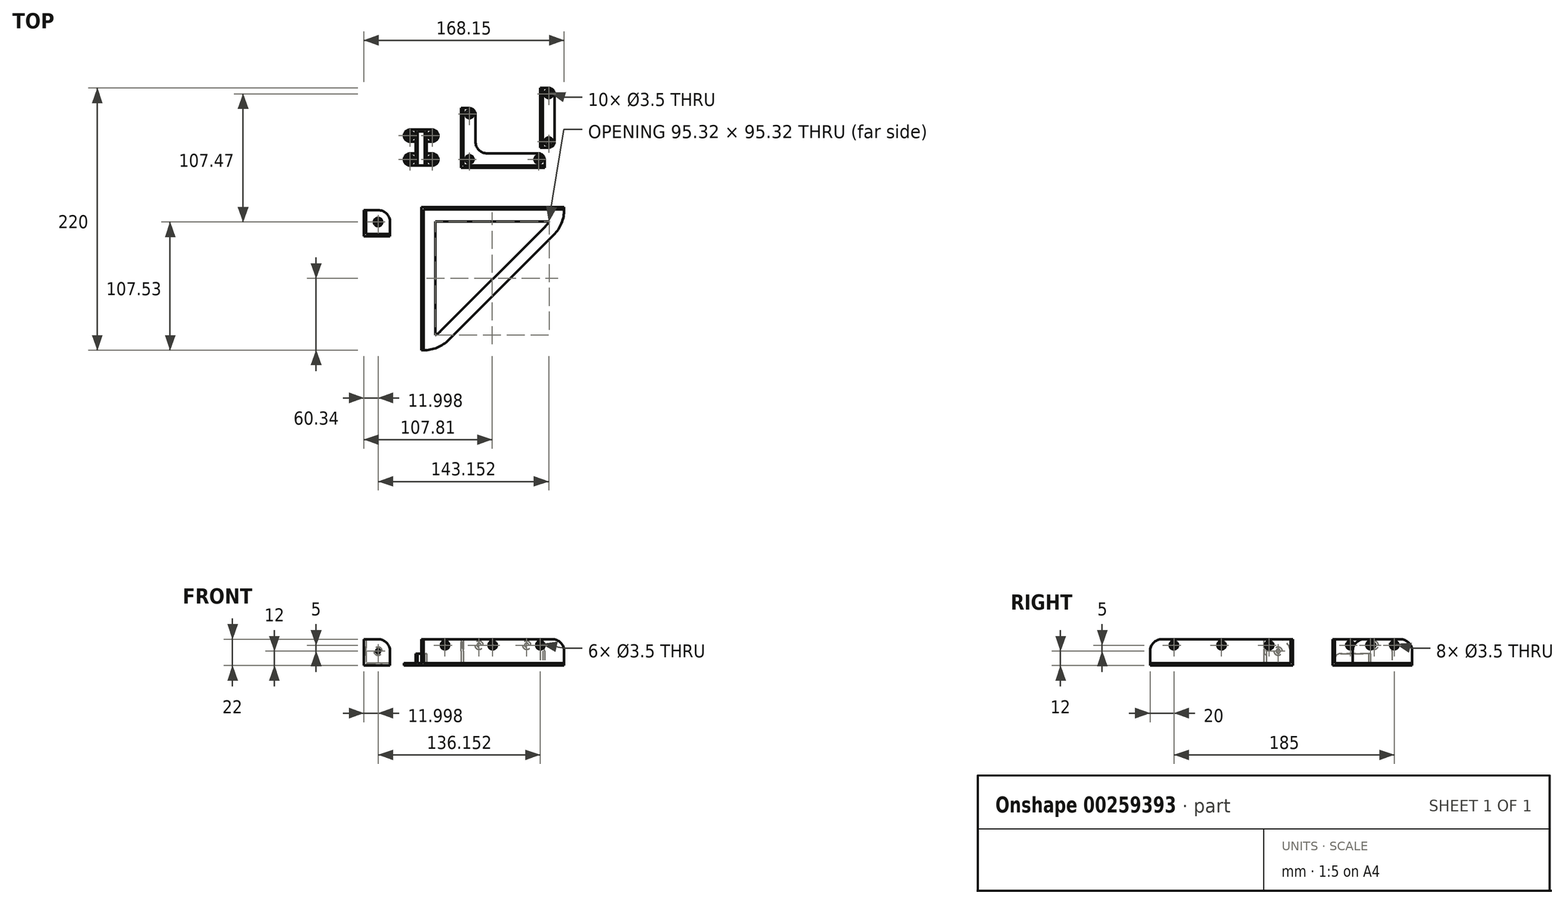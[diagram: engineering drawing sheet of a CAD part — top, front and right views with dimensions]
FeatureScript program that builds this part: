
annotation { "Feature Type Name" : "Feature", "Feature Type Description" : "" }
export const myFeature = defineFeature(function(context is Context, id is Id, definition is map)
    precondition{}
    {
        {
            var Q0;
            Q0=qCreatedBy(makeId("Top.planeOp"),FACE);
            var sketch = newSketch(context, id + "F0", { "sketchPlane" : qUnion([Q0])});
            skLineSegment(sketch, "E0.bottom", {"start": v(-4.5, 15) * mm, "end": v(4.5, 15) * mm});
            skLineSegment(sketch, "E0.top", {"start": v(-4.5, -15) * mm, "end": v(4.5, -15) * mm});
            skLineSegment(sketch, "E0.left", {"start": v(-4.5, 15) * mm, "end": v(-4.5, -15) * mm});
            skLineSegment(sketch, "E0.right", {"start": v(4.5, 15) * mm, "end": v(4.5, -15) * mm});
            skLineSegment(sketch, "E1", {"start": v(-2.9, 13.4) * mm, "end": v(-2.9, -15) * mm});
            skLineSegment(sketch, "E2", {"start": v(2.9, -15) * mm, "end": v(2.9, 13.4) * mm});
            skPoint(sketch, "E3", {"position": v(0, -15) * mm});
            skArc(sketch, "E4", {"start": v(9.5, -15) * mm, "mid": v(14.5, -10) * mm, "end": v(9.5, -5) * mm});
            skLineSegment(sketch, "E5", {"start": v(9.5, -5) * mm, "end": v(4.5, -5) * mm});
            skLineSegment(sketch, "E6", {"start": v(4.5, -15) * mm, "end": v(9.5, -15) * mm});
            skArc(sketch, "E7", {"start": v(9.5, 5) * mm, "mid": v(14.5, 10) * mm, "end": v(9.5, 15) * mm});
            skLineSegment(sketch, "E8", {"start": v(4.5, 15) * mm, "end": v(9.5, 15) * mm});
            skLineSegment(sketch, "E9", {"start": v(9.5, 5) * mm, "end": v(4.5, 5) * mm});
            skLineSegment(sketch, "E10", {"start": v(-2.9, 13.4) * mm, "end": v(2.9, 13.4) * mm});
            skSolve(sketch);
        }
        {
            var Q0;
            Q0 = qSketchRegion(id + "F0", true);
            extrude(context, id + "F1", {"entities" : qUnion([Q0]), "depth" : 2 * mm});
        }
        {
            var Q0;
            {var subQ6=sQuery(id+"F0.wireOp",EDGE,"E0.bottom");Q0=makeQuery(id+"F0.imprint","IMPRINT",FACE,{"disambiguationData":[TD([[makeQuery(id+"F0.imprint","IMPRINT",EDGE,{"derivedFrom":subQ6}),-1.0]])]});}
            extrude(context, id + "F2", {"entities" : qUnion([Q0]), "operationType" : NewBodyOperationType.ADD, "depth" : 10 * mm});
        }
        {
            var Q0;
            {var subQ0=sQuery(id+"F0.wireOp",EDGE,"E9");var subQ1=sQuery(id+"F0.wireOp",EDGE,"E7");var subQ2=sQuery(id+"F0.wireOp",EDGE,"E0.right");var subQ3=sQuery(id+"F0.wireOp",EDGE,"E8");var subQ4=sQuery(id+"F0.wireOp",EDGE,"E0.bottom");Q0=makeQuery(id+"F2.boolean.opBoolean","SPLIT",FACE,{"disambiguationData":[TD([makeQuery(id+"F1.opExtrude","SWEPT_FACE",FACE,{"disambiguationData":[OSD([subQ1])]})])],"derivedFrom":makeQuery(id+"F1.opExtrude","CAP_FACE",FACE,{"disambiguationData":[OSD([subQ4,sQuery(id+"F0.wireOp",EDGE,"E0.top"),sQuery(id+"F0.wireOp",EDGE,"E0.left"),subQ2,sQuery(id+"F0.wireOp",EDGE,"E4"),sQuery(id+"F0.wireOp",EDGE,"E5"),sQuery(id+"F0.wireOp",EDGE,"E6"),subQ1,subQ3,subQ0])],"isStart":false})});}
            var sketch = newSketch(context, id + "F3", { "sketchPlane" : qUnion([Q0])});
            skArc(sketch, "E11.0", {"start": v(9.5, 5) * mm, "mid": v(14.5, 10) * mm, "end": v(9.5, 15) * mm, "construction": true});
            skArc(sketch, "E12.0", {"start": v(9.5, -15) * mm, "mid": v(14.5, -10) * mm, "end": v(9.5, -5) * mm, "construction": true});
            skSolve(sketch);
        }
        {
            var Q0;
            {var subQ0=sQuery(id+"F0.wireOp",EDGE,"E0.top");Q0=makeQuery(id+"F2.opExtrude","CAP_EDGE",EDGE,{"disambiguationData":[OSD([subQ0]),TDD([makeQuery(id+"F0.imprint","IMPRINT",EDGE,{"disambiguationData":[TD([[makeQuery(id+"F0.imprint","INTERSECT",VERTEX,{"derivedFrom":[subQ0,sQuery(id+"F0.wireOp",EDGE,"E0.left")]}),-1.0]])],"derivedFrom":subQ0})])],"isStart":false});}
            var Q1;
            {var subQ0=sQuery(id+"F0.wireOp",EDGE,"E0.top");Q1=makeQuery(id+"F2.opExtrude","CAP_EDGE",EDGE,{"disambiguationData":[OSD([subQ0]),TDD([makeQuery(id+"F0.imprint","IMPRINT",EDGE,{"disambiguationData":[TD([[makeQuery(id+"F0.imprint","INTERSECT",VERTEX,{"derivedFrom":[subQ0,sQuery(id+"F0.wireOp",EDGE,"E2")]}),-1.0]])],"derivedFrom":subQ0})])],"isStart":false});}
            fillet(context, id + "F4", {"entities" : qUnion([Q0, Q1]), "radius" : 5 * mm, "tangentPropagation" : true, "allowEdgeOverflow" : false});
        }
        {
            var Q0;
            Q0=makeQuery(id+"F2.opExtrude","SWEPT_EDGE",EDGE,{"disambiguationData":[OSD([sQuery(id+"F0.wireOp",EDGE,"E0.bottom"),sQuery(id+"F0.wireOp",EDGE,"E0.right"),sQuery(id+"F0.wireOp",EDGE,"E8")])]});
            var Q1;
            {var subQ0=sQuery(id+"F0.wireOp",EDGE,"E0.left");var subQ1=sQuery(id+"F0.wireOp",EDGE,"E0.bottom");Q1=makeQuery(id+"F2.boolean.opBoolean","MERGE",EDGE,{"derivedFrom":[makeQuery(id+"F1.opExtrude","SWEPT_EDGE",EDGE,{"disambiguationData":[OSD([subQ1,subQ0])]}),makeQuery(id+"F2.opExtrude","SWEPT_EDGE",EDGE,{"disambiguationData":[OSD([subQ1,subQ0])]})]});}
            fillet(context, id + "F5", {"entities" : qUnion([Q0, Q1]), "radius" : 1 * mm, "tangentPropagation" : true, "allowEdgeOverflow" : false});
        }
        {
            var Q0;
            Q0=sQuery(id+"F3.wireOp",VERTEX,"E11.0.center");
            var Q1;
            Q1=sQuery(id+"F3.wireOp",VERTEX,"E12.0.center");
            var Q2;
            Q2=makeQuery(id+"F1.opExtrude","SWEPT_BODY",BODY,{"disambiguationData":[OSD([sQuery(id+"F0.wireOp",EDGE,"E0.bottom"),sQuery(id+"F0.wireOp",EDGE,"E0.top"),sQuery(id+"F0.wireOp",EDGE,"E0.left"),sQuery(id+"F0.wireOp",EDGE,"E0.right"),sQuery(id+"F0.wireOp",EDGE,"E4"),sQuery(id+"F0.wireOp",EDGE,"E5"),sQuery(id+"F0.wireOp",EDGE,"E6"),sQuery(id+"F0.wireOp",EDGE,"E7"),sQuery(id+"F0.wireOp",EDGE,"E8"),sQuery(id+"F0.wireOp",EDGE,"E9")])]});
            hole(context, id + "F6", {"style" : HoleStyle.C_SINK, "endStyle" : HoleEndStyle.BLIND, "holeDiameter" : 3.5 * mm, "cSinkDiameter" : 7 * mm, "cSinkAngle" : 90 * degree, "holeDepth" : 20 * mm, "tappedDepth" : 12 * mm, "tapClearance" : 3, "locations" : qUnion([Q0, Q1]), "scope" : qUnion([Q2])});
        }
        {
            var Q0;
            Q0=makeQuery(id+"F1.opExtrude","SWEPT_BODY",BODY,{"disambiguationData":[OSD([sQuery(id+"F0.wireOp",EDGE,"E0.bottom"),sQuery(id+"F0.wireOp",EDGE,"E0.top"),sQuery(id+"F0.wireOp",EDGE,"E0.left"),sQuery(id+"F0.wireOp",EDGE,"E0.right"),sQuery(id+"F0.wireOp",EDGE,"E4"),sQuery(id+"F0.wireOp",EDGE,"E5"),sQuery(id+"F0.wireOp",EDGE,"E6"),sQuery(id+"F0.wireOp",EDGE,"E7"),sQuery(id+"F0.wireOp",EDGE,"E8"),sQuery(id+"F0.wireOp",EDGE,"E9")])]});
            var Q1;
            Q1=qCreatedBy(makeId("Right.planeOp"),FACE);
            mirror(context, id + "F7", {"entities" : qUnion([Q0]), "mirrorPlane" : qUnion([Q1])});
        }
        {
            var Q0;
            Q0=qCreatedBy(makeId("Top.planeOp"),FACE);
            var sketch = newSketch(context, id + "F8", { "sketchPlane" : qUnion([Q0])});
            skLineSegment(sketch, "E13.bottom", {"start": v(33.53, 33.08) * mm, "end": v(40.53, 33.08) * mm});
            skLineSegment(sketch, "E13.top", {"start": v(33.53, -16.92) * mm, "end": v(103.53, -16.92) * mm});
            skLineSegment(sketch, "E13.left", {"start": v(33.53, 33.08) * mm, "end": v(33.53, -16.92) * mm});
            skLineSegment(sketch, "E13.right", {"start": v(103.53, -9.92) * mm, "end": v(103.53, -16.92) * mm});
            skPoint(sketch, "E14", {"position": v(40.53, 28.08) * mm});
            skPoint(sketch, "E15", {"position": v(98.53, -9.92) * mm});
            skCircle(sketch, "E16", {"center": v(40.53, 28.08) * mm, "radius": 3.5 * mm, "construction": true});
            skCircle(sketch, "E17", {"center": v(98.53, -9.92) * mm, "radius": 3.5 * mm, "construction": true});
            skArc(sketch, "E18", {"start": v(45.53, 28.08) * mm, "mid": v(44.06, 31.61) * mm, "end": v(40.53, 33.08) * mm});
            skArc(sketch, "E19", {"start": v(103.53, -9.92) * mm, "mid": v(102.06, -6.39) * mm, "end": v(98.53, -4.92) * mm});
            skLineSegment(sketch, "E20", {"start": v(45.53, 28.08) * mm, "end": v(45.53, 5.08) * mm});
            skLineSegment(sketch, "E21", {"start": v(98.53, -4.92) * mm, "end": v(55.53, -4.92) * mm});
            skArc(sketch, "E22", {"start": v(45.53, 5.08) * mm, "mid": v(48.46, -2) * mm, "end": v(55.53, -4.92) * mm});
            skLineSegment(sketch, "E23", {"start": v(35.53, 33.08) * mm, "end": v(35.53, -14.92) * mm});
            skLineSegment(sketch, "E24", {"start": v(35.53, -14.92) * mm, "end": v(103.53, -14.92) * mm});
            skPoint(sketch, "E25", {"position": v(40.53, -9.92) * mm});
            skCircle(sketch, "E26", {"center": v(40.53, -9.92) * mm, "radius": 3.5 * mm, "construction": true});
            skLineSegment(sketch, "E27.bottom", {"start": v(100, 50) * mm, "end": v(107, 50) * mm});
            skLineSegment(sketch, "E27.top", {"start": v(100, 0) * mm, "end": v(107, 0) * mm});
            skLineSegment(sketch, "E27.left", {"start": v(100, 50) * mm, "end": v(100, 0) * mm});
            skLineSegment(sketch, "E27.right", {"start": v(112, 45) * mm, "end": v(112, 5) * mm});
            skPoint(sketch, "E28.visualSharp", {"position": v(112, 50) * mm});
            skArc(sketch, "E28.filletArc", {"start": v(112, 45) * mm, "mid": v(110.54, 48.54) * mm, "end": v(107, 50) * mm});
            skPoint(sketch, "E29.visualSharp", {"position": v(112, 0) * mm});
            skArc(sketch, "E29.filletArc", {"start": v(107, 0) * mm, "mid": v(110.54, 1.46) * mm, "end": v(112, 5) * mm});
            skLineSegment(sketch, "E30", {"start": v(102, 50) * mm, "end": v(102, 0) * mm});
            skCircle(sketch, "E31", {"center": v(107, 5) * mm, "radius": 3.5 * mm, "construction": true});
            skCircle(sketch, "E32", {"center": v(107, 45) * mm, "radius": 3.5 * mm, "construction": true});
            skSolve(sketch);
        }
        {
            var Q0;
            Q0=qCreatedBy(makeId("Top.planeOp"),FACE);
            var sketch = newSketch(context, id + "F9", { "sketchPlane" : qUnion([Q0])});
            skLineSegment(sketch, "E33.bottom", {"start": v(0, -50) * mm, "end": v(120, -50) * mm});
            skLineSegment(sketch, "E33.top", {"start": v(0, -170) * mm, "end": v(2, -170) * mm});
            skLineSegment(sketch, "E33.left", {"start": v(0, -50) * mm, "end": v(0, -170) * mm});
            skLineSegment(sketch, "E33.right", {"start": v(120, -50) * mm, "end": v(120, -52) * mm});
            skLineSegment(sketch, "E34", {"start": v(2, -170) * mm, "end": v(2, -52) * mm});
            skLineSegment(sketch, "E35", {"start": v(2, -52) * mm, "end": v(120, -52) * mm});
            skArc(sketch, "E36", {"start": v(2, -170) * mm, "mid": v(13.48, -167.72) * mm, "end": v(23.21, -161.21) * mm});
            skArc(sketch, "E37", {"start": v(111.21, -73.21) * mm, "mid": v(117.72, -63.48) * mm, "end": v(120, -52) * mm});
            skLineSegment(sketch, "E38", {"start": v(23.21, -161.21) * mm, "end": v(111.21, -73.21) * mm});
            skArc(sketch, "E39.0", {"start": v(104.14, -66.14) * mm, "mid": v(105.87, -64.18) * mm, "end": v(107.32, -62) * mm});
            skLineSegment(sketch, "E39.1", {"start": v(16.14, -154.14) * mm, "end": v(104.14, -66.14) * mm});
            skArc(sketch, "E39.2", {"start": v(12, -157.32) * mm, "mid": v(14.18, -155.87) * mm, "end": v(16.14, -154.14) * mm});
            skLineSegment(sketch, "E40", {"start": v(12, -62) * mm, "end": v(12, -157.32) * mm});
            skLineSegment(sketch, "E41", {"start": v(12, -62) * mm, "end": v(107.32, -62) * mm});
            skSolve(sketch);
        }
        {
            var Q0;
            Q0=qCreatedBy(makeId("Top.planeOp"),FACE);
            var sketch = newSketch(context, id + "F10", { "sketchPlane" : qUnion([Q0])});
            skLineSegment(sketch, "E42.bottom", {"start": v(-48.15, -74.47) * mm, "end": v(-26.15, -74.47) * mm});
            skLineSegment(sketch, "E42.top", {"start": v(-48.15, -52.47) * mm, "end": v(-36.15, -52.47) * mm});
            skLineSegment(sketch, "E42.left", {"start": v(-48.15, -74.47) * mm, "end": v(-48.15, -52.47) * mm});
            skLineSegment(sketch, "E42.right", {"start": v(-26.15, -74.47) * mm, "end": v(-26.15, -62.47) * mm});
            skLineSegment(sketch, "E43", {"start": v(-26.15, -72.47) * mm, "end": v(-46.15, -72.47) * mm});
            skLineSegment(sketch, "E44", {"start": v(-46.15, -72.47) * mm, "end": v(-46.15, -52.47) * mm});
            skPoint(sketch, "E45.visualSharp", {"position": v(-26.15, -52.47) * mm});
            skArc(sketch, "E45.filletArc", {"start": v(-26.15, -62.47) * mm, "mid": v(-29.08, -55.4) * mm, "end": v(-36.15, -52.47) * mm});
            skCircle(sketch, "E46", {"center": v(-36.15, -62.47) * mm, "radius": 3.5 * mm, "construction": true});
            skSolve(sketch);
        }
        {
            var Q0;
            {var subQ3=sQuery(id+"F8.wireOp",EDGE,"E18");Q0=makeQuery(id+"F8.imprint","IMPRINT",FACE,{"disambiguationData":[TD([[makeQuery(id+"F8.imprint","IMPRINT",EDGE,{"derivedFrom":subQ3}),1.0]])]});}
            var Q1;
            Q1=makeQuery(id+"F8.imprint","IMPRINT",FACE,{"disambiguationData":[TD([[makeQuery(id+"F8.imprint","IMPRINT",EDGE,{"derivedFrom":sQuery(id+"F8.wireOp",EDGE,"E27.right")}),-1.0]])]});
            var Q2;
            Q2=makeQuery(id+"F9.imprint","IMPRINT",FACE,{"disambiguationData":[TD([[makeQuery(id+"F9.imprint","IMPRINT",EDGE,{"derivedFrom":sQuery(id+"F9.wireOp",EDGE,"E34")}),-1.0]])]});
            var Q3;
            {var subQ0=sQuery(id+"F10.wireOp",EDGE,"E43");Q3=makeQuery(id+"F10.imprint","IMPRINT",FACE,{"disambiguationData":[TD([[makeQuery(id+"F10.imprint","IMPRINT",EDGE,{"derivedFrom":subQ0}),-1.0]])]});}
            var Q4;
            Q4=sQuery(id+"F8.wireOp",EDGE,"E23");
            extrude(context, id + "F11", {"entities" : qUnion([Q0, Q1, Q2, Q3]), "surfaceEntities" : qUnion([Q4]), "depth" : 2 * mm});
        }
        {
            var Q0;
            {var subQ1=sQuery(id+"F8.wireOp",EDGE,"E13.top");Q0=makeQuery(id+"F8.imprint","IMPRINT",FACE,{"disambiguationData":[TD([[makeQuery(id+"F8.imprint","IMPRINT",EDGE,{"derivedFrom":subQ1}),1.0]])]});}
            var Q1;
            {var subQ0=sQuery(id+"F8.wireOp",EDGE,"E27.left");Q1=makeQuery(id+"F8.imprint","IMPRINT",FACE,{"disambiguationData":[TD([[makeQuery(id+"F8.imprint","IMPRINT",EDGE,{"derivedFrom":subQ0}),1.0]])]});}
            var Q2;
            Q2=makeQuery(id+"F9.imprint","IMPRINT",FACE,{"disambiguationData":[TD([[makeQuery(id+"F9.imprint","IMPRINT",EDGE,{"derivedFrom":sQuery(id+"F9.wireOp",EDGE,"E33.bottom")}),-1.0]])]});
            var Q3;
            {var subQ1=sQuery(id+"F10.wireOp",EDGE,"E42.bottom");Q3=makeQuery(id+"F10.imprint","IMPRINT",FACE,{"disambiguationData":[TD([[makeQuery(id+"F10.imprint","IMPRINT",EDGE,{"derivedFrom":subQ1}),1.0]])]});}
            extrude(context, id + "F12", {"entities" : qUnion([Q0, Q1, Q2, Q3]), "operationType" : NewBodyOperationType.ADD, "depth" : 22 * mm});
        }
        {
            var Q0;
            Q0=makeQuery(id+"F12.opExtrude","CAP_EDGE",EDGE,{"disambiguationData":[OSD([sQuery(id+"F8.wireOp",EDGE,"E13.bottom")])],"isStart":false});
            var Q1;
            Q1=makeQuery(id+"F12.opExtrude","CAP_EDGE",EDGE,{"disambiguationData":[OSD([sQuery(id+"F8.wireOp",EDGE,"E13.right")])],"isStart":false});
            var Q2;
            Q2=makeQuery(id+"F12.opExtrude","CAP_EDGE",EDGE,{"disambiguationData":[OSD([sQuery(id+"F8.wireOp",EDGE,"E27.bottom")])],"isStart":false});
            var Q3;
            Q3=makeQuery(id+"F12.opExtrude","CAP_EDGE",EDGE,{"disambiguationData":[OSD([sQuery(id+"F8.wireOp",EDGE,"E27.top")])],"isStart":false});
            var Q4;
            Q4=makeQuery(id+"F12.opExtrude","CAP_EDGE",EDGE,{"disambiguationData":[OSD([sQuery(id+"F9.wireOp",EDGE,"E33.top")])],"isStart":false});
            var Q5;
            Q5=makeQuery(id+"F12.opExtrude","CAP_EDGE",EDGE,{"disambiguationData":[OSD([sQuery(id+"F9.wireOp",EDGE,"E33.right")])],"isStart":false});
            var Q6;
            Q6=makeQuery(id+"F12.opExtrude","CAP_EDGE",EDGE,{"disambiguationData":[OSD([sQuery(id+"F10.wireOp",EDGE,"E42.right")])],"isStart":false});
            var Q7;
            Q7=makeQuery(id+"F12.opExtrude","CAP_EDGE",EDGE,{"disambiguationData":[OSD([sQuery(id+"F10.wireOp",EDGE,"E42.top")])],"isStart":false});
            fillet(context, id + "F13", {"entities" : qUnion([Q0, Q1, Q2, Q3, Q4, Q5, Q6, Q7]), "radius" : 10 * mm, "tangentPropagation" : true, "allowEdgeOverflow" : false});
        }
        {
            var Q0;
            Q0=makeQuery(id+"F12.opExtrude","SWEPT_FACE",FACE,{"disambiguationData":[OSD([sQuery(id+"F8.wireOp",EDGE,"E23")])]});
            var sketch = newSketch(context, id + "F14", { "sketchPlane" : qUnion([Q0])});
            skPoint(sketch, "E47", {"position": v(18.08, 17) * mm});
            skPoint(sketch, "E48", {"position": v(-1.92, 17) * mm});
            skLineSegment(sketch, "E49", {"start": v(45.41, 17) * mm, "end": v(7.06, 17) * mm, "construction": true});
            skCircle(sketch, "E50", {"center": v(18.08, 17) * mm, "radius": 3.5 * mm, "construction": true});
            skCircle(sketch, "E51", {"center": v(-1.92, 17) * mm, "radius": 3.5 * mm, "construction": true});
            skSolve(sketch);
        }
        {
            var Q0;
            Q0=makeQuery(id+"F12.opExtrude","SWEPT_FACE",FACE,{"disambiguationData":[OSD([sQuery(id+"F8.wireOp",EDGE,"E24")])]});
            var sketch = newSketch(context, id + "F15", { "sketchPlane" : qUnion([Q0])});
            skLineSegment(sketch, "E52", {"start": v(-73.47, 17) * mm, "end": v(-33.05, 17) * mm, "construction": true});
            skPoint(sketch, "E53", {"position": v(-88.53, 17) * mm});
            skPoint(sketch, "E54", {"position": v(-48.53, 17) * mm});
            skCircle(sketch, "E55", {"center": v(-88.53, 17) * mm, "radius": 3.5 * mm, "construction": true});
            skCircle(sketch, "E56", {"center": v(-48.53, 17) * mm, "radius": 3.5 * mm, "construction": true});
            skSolve(sketch);
        }
        {
            var Q0;
            Q0=makeQuery(id+"F11.opExtrude","CAP_FACE",FACE,{"disambiguationData":[OSD([sQuery(id+"F8.wireOp",EDGE,"E13.bottom"),sQuery(id+"F8.wireOp",EDGE,"E13.right"),sQuery(id+"F8.wireOp",EDGE,"E18"),sQuery(id+"F8.wireOp",EDGE,"E19"),sQuery(id+"F8.wireOp",EDGE,"E20"),sQuery(id+"F8.wireOp",EDGE,"E21"),sQuery(id+"F8.wireOp",EDGE,"E22"),sQuery(id+"F8.wireOp",EDGE,"E23"),sQuery(id+"F8.wireOp",EDGE,"E24")])],"isStart":false});
            var sketch = newSketch(context, id + "F16", { "sketchPlane" : qUnion([Q0])});
            skPoint(sketch, "E57.0", {"position": v(98.53, -9.92) * mm});
            skPoint(sketch, "E57.1", {"position": v(40.53, 28.08) * mm});
            skCircle(sketch, "E58.0", {"center": v(40.53, 28.08) * mm, "radius": 3.5 * mm, "construction": true});
            skCircle(sketch, "E58.1", {"center": v(98.53, -9.92) * mm, "radius": 3.5 * mm, "construction": true});
            skPoint(sketch, "E59.0", {"position": v(40.53, -9.92) * mm});
            skCircle(sketch, "E59.1", {"center": v(40.53, -9.92) * mm, "radius": 3.5 * mm, "construction": true});
            skCircle(sketch, "E60.0", {"center": v(107, 45) * mm, "radius": 3.5 * mm, "construction": true});
            skPoint(sketch, "E60.1", {"position": v(107, 45) * mm});
            skCircle(sketch, "E60.2", {"center": v(107, 5) * mm, "radius": 3.5 * mm, "construction": true});
            skPoint(sketch, "E60.3", {"position": v(107, 5) * mm});
            skSolve(sketch);
        }
        {
            var Q0;
            Q0=makeQuery(id+"F12.opExtrude","SWEPT_FACE",FACE,{"disambiguationData":[OSD([sQuery(id+"F8.wireOp",EDGE,"E30")])]});
            var sketch = newSketch(context, id + "F17", { "sketchPlane" : qUnion([Q0])});
            skLineSegment(sketch, "E61", {"start": v(10.1, 17) * mm, "end": v(39.65, 17) * mm, "construction": true});
            skPoint(sketch, "E62", {"position": v(15, 17) * mm});
            skPoint(sketch, "E63", {"position": v(35, 17) * mm});
            skCircle(sketch, "E64", {"center": v(15, 17) * mm, "radius": 3.5 * mm, "construction": true});
            skCircle(sketch, "E65", {"center": v(35, 17) * mm, "radius": 3.5 * mm, "construction": true});
            skSolve(sketch);
        }
        {
            var Q0;
            Q0=makeQuery(id+"F12.opExtrude","SWEPT_FACE",FACE,{"disambiguationData":[OSD([sQuery(id+"F9.wireOp",EDGE,"E35")])]});
            var sketch = newSketch(context, id + "F18", { "sketchPlane" : qUnion([Q0])});
            skLineSegment(sketch, "E66", {"start": v(-8.28, 17) * mm, "end": v(115.12, 17) * mm, "construction": true});
            skPoint(sketch, "E67", {"position": v(20, 17) * mm});
            skPoint(sketch, "E68", {"position": v(60, 17) * mm});
            skPoint(sketch, "E69", {"position": v(100, 17) * mm});
            skCircle(sketch, "E70", {"center": v(20, 17) * mm, "radius": 3.5 * mm, "construction": true});
            skCircle(sketch, "E71", {"center": v(60, 17) * mm, "radius": 3.5 * mm, "construction": true});
            skCircle(sketch, "E72", {"center": v(100, 17) * mm, "radius": 3.5 * mm, "construction": true});
            skSolve(sketch);
        }
        {
            var Q0;
            Q0=makeQuery(id+"F12.opExtrude","SWEPT_FACE",FACE,{"disambiguationData":[OSD([sQuery(id+"F9.wireOp",EDGE,"E34")])]});
            var sketch = newSketch(context, id + "F19", { "sketchPlane" : qUnion([Q0])});
            skLineSegment(sketch, "E73", {"start": v(-164.14, 17) * mm, "end": v(-60.4, 17) * mm, "construction": true});
            skPoint(sketch, "E74", {"position": v(-150, 17) * mm});
            skPoint(sketch, "E75", {"position": v(-110, 17) * mm});
            skPoint(sketch, "E76", {"position": v(-70, 17) * mm});
            skCircle(sketch, "E77", {"center": v(-150, 17) * mm, "radius": 3.5 * mm, "construction": true});
            skCircle(sketch, "E78", {"center": v(-110, 17) * mm, "radius": 3.5 * mm, "construction": true});
            skCircle(sketch, "E79", {"center": v(-70, 17) * mm, "radius": 3.5 * mm, "construction": true});
            skSolve(sketch);
        }
        {
            var Q0;
            Q0=makeQuery(id+"F12.opExtrude","SWEPT_FACE",FACE,{"disambiguationData":[OSD([sQuery(id+"F10.wireOp",EDGE,"E44")])]});
            var sketch = newSketch(context, id + "F20", { "sketchPlane" : qUnion([Q0])});
            skArc(sketch, "E80.0", {"start": v(-52.47, 12) * mm, "mid": v(-55.4, 19.07) * mm, "end": v(-62.47, 22) * mm, "construction": true});
            skLineSegment(sketch, "E80.1", {"start": v(-72.47, 22) * mm, "end": v(-62.47, 22) * mm, "construction": true});
            skLineSegment(sketch, "E80.2", {"start": v(-72.47, 22) * mm, "end": v(-72.47, 2) * mm, "construction": true});
            skLineSegment(sketch, "E80.3", {"start": v(-72.47, 2) * mm, "end": v(-52.47, 2) * mm, "construction": true});
            skLineSegment(sketch, "E80.4", {"start": v(-52.47, 12) * mm, "end": v(-52.47, 2) * mm, "construction": true});
            skSolve(sketch);
        }
        {
            var Q0;
            Q0=makeQuery(id+"F11.opExtrude","CAP_FACE",FACE,{"disambiguationData":[OSD([sQuery(id+"F10.wireOp",EDGE,"E42.top"),sQuery(id+"F10.wireOp",EDGE,"E42.right"),sQuery(id+"F10.wireOp",EDGE,"E43"),sQuery(id+"F10.wireOp",EDGE,"E44"),sQuery(id+"F10.wireOp",EDGE,"E45.filletArc")])],"isStart":false});
            var sketch = newSketch(context, id + "F21", { "sketchPlane" : qUnion([Q0])});
            skArc(sketch, "E81.0", {"start": v(-26.15, -62.47) * mm, "mid": v(-29.08, -55.4) * mm, "end": v(-36.15, -52.47) * mm, "construction": true});
            skPoint(sketch, "E81.1", {"position": v(-36.15, -62.47) * mm});
            skSolve(sketch);
        }
        {
            var Q0;
            Q0=makeQuery(id+"F12.opExtrude","SWEPT_FACE",FACE,{"disambiguationData":[OSD([sQuery(id+"F10.wireOp",EDGE,"E43")])]});
            var sketch = newSketch(context, id + "F22", { "sketchPlane" : qUnion([Q0])});
            skArc(sketch, "E82.0", {"start": v(36.15, 22) * mm, "mid": v(29.08, 19.07) * mm, "end": v(26.15, 12) * mm, "construction": true});
            skSolve(sketch);
        }
        {
            var Q0;
            Q0=sQuery(id+"F14.wireOp",VERTEX,"E47");
            var Q1;
            Q1=sQuery(id+"F15.wireOp",VERTEX,"E54");
            var Q2;
            Q2=sQuery(id+"F15.wireOp",VERTEX,"E53");
            var Q3;
            Q3=sQuery(id+"F14.wireOp",VERTEX,"E48");
            var Q4;
            Q4=sQuery(id+"F16.wireOp",VERTEX,"E57.0");
            var Q5;
            Q5=sQuery(id+"F16.wireOp",VERTEX,"E57.1");
            var Q6;
            Q6=sQuery(id+"F16.wireOp",VERTEX,"E59.0");
            var Q7;
            Q7=sQuery(id+"F16.wireOp",VERTEX,"E60.3");
            var Q8;
            Q8=sQuery(id+"F16.wireOp",VERTEX,"E60.1");
            var Q9;
            Q9=sQuery(id+"F17.wireOp",VERTEX,"E63");
            var Q10;
            Q10=sQuery(id+"F17.wireOp",VERTEX,"E62");
            var Q11;
            Q11=sQuery(id+"F19.wireOp",VERTEX,"E76");
            var Q12;
            Q12=sQuery(id+"F19.wireOp",VERTEX,"E75");
            var Q13;
            Q13=sQuery(id+"F19.wireOp",VERTEX,"E74");
            var Q14;
            Q14=sQuery(id+"F18.wireOp",VERTEX,"E67");
            var Q15;
            Q15=sQuery(id+"F18.wireOp",VERTEX,"E68");
            var Q16;
            Q16=sQuery(id+"F18.wireOp",VERTEX,"E69");
            var Q17;
            Q17=sQuery(id+"F20.wireOp",VERTEX,"E80.0.center");
            var Q18;
            Q18=sQuery(id+"F22.wireOp",VERTEX,"E82.0.center");
            var Q19;
            Q19=sQuery(id+"F21.wireOp",VERTEX,"E81.1");
            var Q20;
            Q20=makeQuery(id+"F11.opExtrude","SWEPT_BODY",BODY,{"disambiguationData":[OSD([sQuery(id+"F8.wireOp",EDGE,"E13.bottom"),sQuery(id+"F8.wireOp",EDGE,"E13.right"),sQuery(id+"F8.wireOp",EDGE,"E18"),sQuery(id+"F8.wireOp",EDGE,"E19"),sQuery(id+"F8.wireOp",EDGE,"E20"),sQuery(id+"F8.wireOp",EDGE,"E21"),sQuery(id+"F8.wireOp",EDGE,"E22"),sQuery(id+"F8.wireOp",EDGE,"E23"),sQuery(id+"F8.wireOp",EDGE,"E24")])]});
            var Q21;
            Q21=makeQuery(id+"F11.opExtrude","SWEPT_BODY",BODY,{"disambiguationData":[OSD([sQuery(id+"F8.wireOp",EDGE,"E27.bottom"),sQuery(id+"F8.wireOp",EDGE,"E27.top"),sQuery(id+"F8.wireOp",EDGE,"E27.right"),sQuery(id+"F8.wireOp",EDGE,"E28.filletArc"),sQuery(id+"F8.wireOp",EDGE,"E29.filletArc"),sQuery(id+"F8.wireOp",EDGE,"E30")])]});
            var Q22;
            Q22=makeQuery(id+"F11.opExtrude","SWEPT_BODY",BODY,{"disambiguationData":[OSD([sQuery(id+"F9.wireOp",EDGE,"E34"),sQuery(id+"F9.wireOp",EDGE,"E35"),sQuery(id+"F9.wireOp",EDGE,"E36"),sQuery(id+"F9.wireOp",EDGE,"E37"),sQuery(id+"F9.wireOp",EDGE,"E38"),sQuery(id+"F9.wireOp",EDGE,"E39.0"),sQuery(id+"F9.wireOp",EDGE,"E39.1"),sQuery(id+"F9.wireOp",EDGE,"E39.2"),sQuery(id+"F9.wireOp",EDGE,"E40"),sQuery(id+"F9.wireOp",EDGE,"E41")])]});
            var Q23;
            Q23=makeQuery(id+"F11.opExtrude","SWEPT_BODY",BODY,{"disambiguationData":[OSD([sQuery(id+"F10.wireOp",EDGE,"E42.top"),sQuery(id+"F10.wireOp",EDGE,"E42.right"),sQuery(id+"F10.wireOp",EDGE,"E43"),sQuery(id+"F10.wireOp",EDGE,"E44"),sQuery(id+"F10.wireOp",EDGE,"E45.filletArc")])]});
            hole(context, id + "F23", {"style" : HoleStyle.C_SINK, "endStyle" : HoleEndStyle.BLIND, "holeDiameter" : 3.5 * mm, "cSinkDiameter" : 7 * mm, "cSinkAngle" : 90 * degree, "holeDepth" : 20 * mm, "tappedDepth" : 12 * mm, "tapClearance" : 3, "startFromSketch" : true, "locations" : qUnion([Q0, Q1, Q2, Q3, Q4, Q5, Q6, Q7, Q8, Q9, Q10, Q11, Q12, Q13, Q14, Q15, Q16, Q17, Q18, Q19]), "scope" : qUnion([Q20, Q21, Q22, Q23])});
        }
    });
